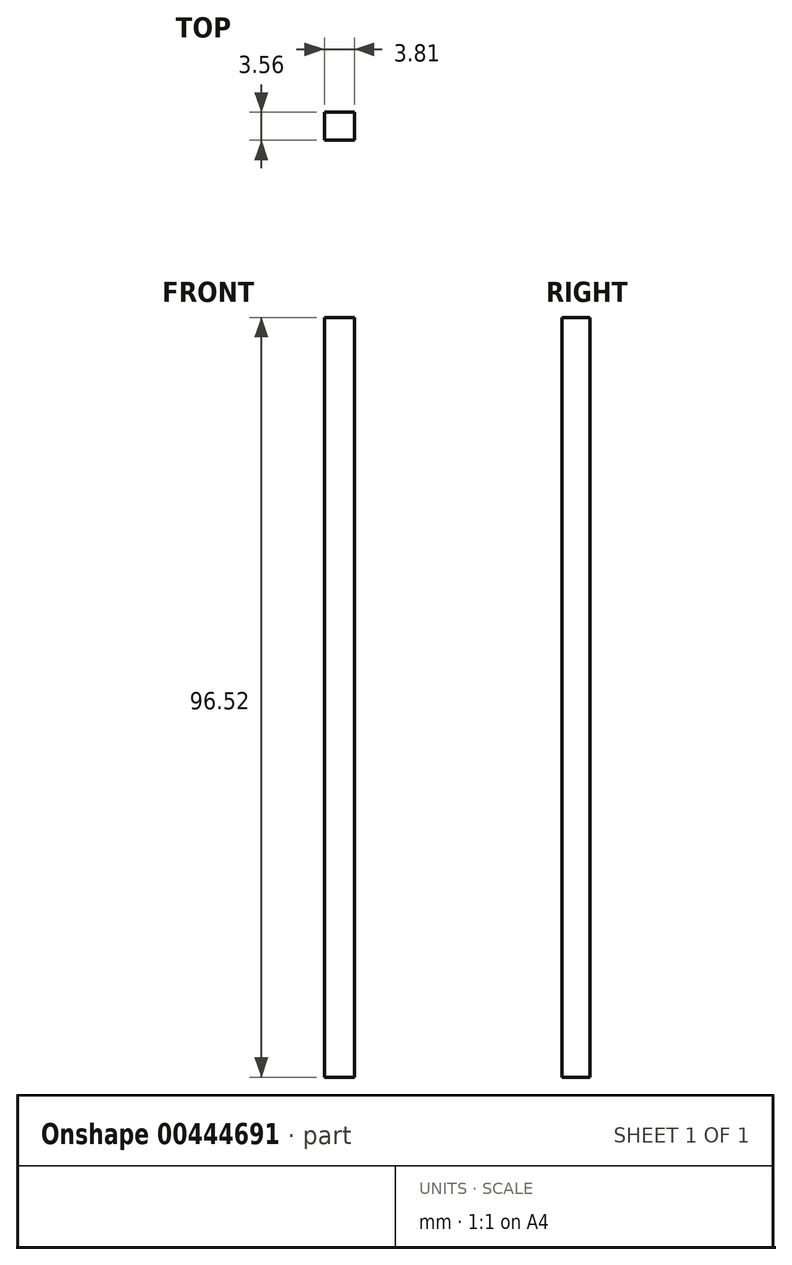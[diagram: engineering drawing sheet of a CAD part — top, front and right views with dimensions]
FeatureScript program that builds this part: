
annotation { "Feature Type Name" : "Feature", "Feature Type Description" : "" }
export const myFeature = defineFeature(function(context is Context, id is Id, definition is map)
    precondition{}
    {
        {
            var Q0;
            Q0=qCreatedBy(makeId("Front.planeOp"),FACE);
            var sketch = newSketch(context, id + "F0", { "sketchPlane" : qUnion([Q0])});
            skLineSegment(sketch, "E0.bottom", {"start": v(-22.5, 63.9) * mm, "end": v(-18.7, 63.9) * mm});
            skLineSegment(sketch, "E0.top", {"start": v(-22.5, -32.61) * mm, "end": v(-18.7, -32.61) * mm});
            skLineSegment(sketch, "E0.left", {"start": v(-22.5, 63.9) * mm, "end": v(-22.5, -32.61) * mm});
            skLineSegment(sketch, "E0.right", {"start": v(-18.7, 63.9) * mm, "end": v(-18.7, -32.61) * mm});
            skSolve(sketch);
        }
        {
            var Q0;
            Q0 = qSketchRegion(id + "F0", true);
            extrude(context, id + "F1", {"entities" : qUnion([Q0]), "depth" : 3.56 * mm});
        }
    });
